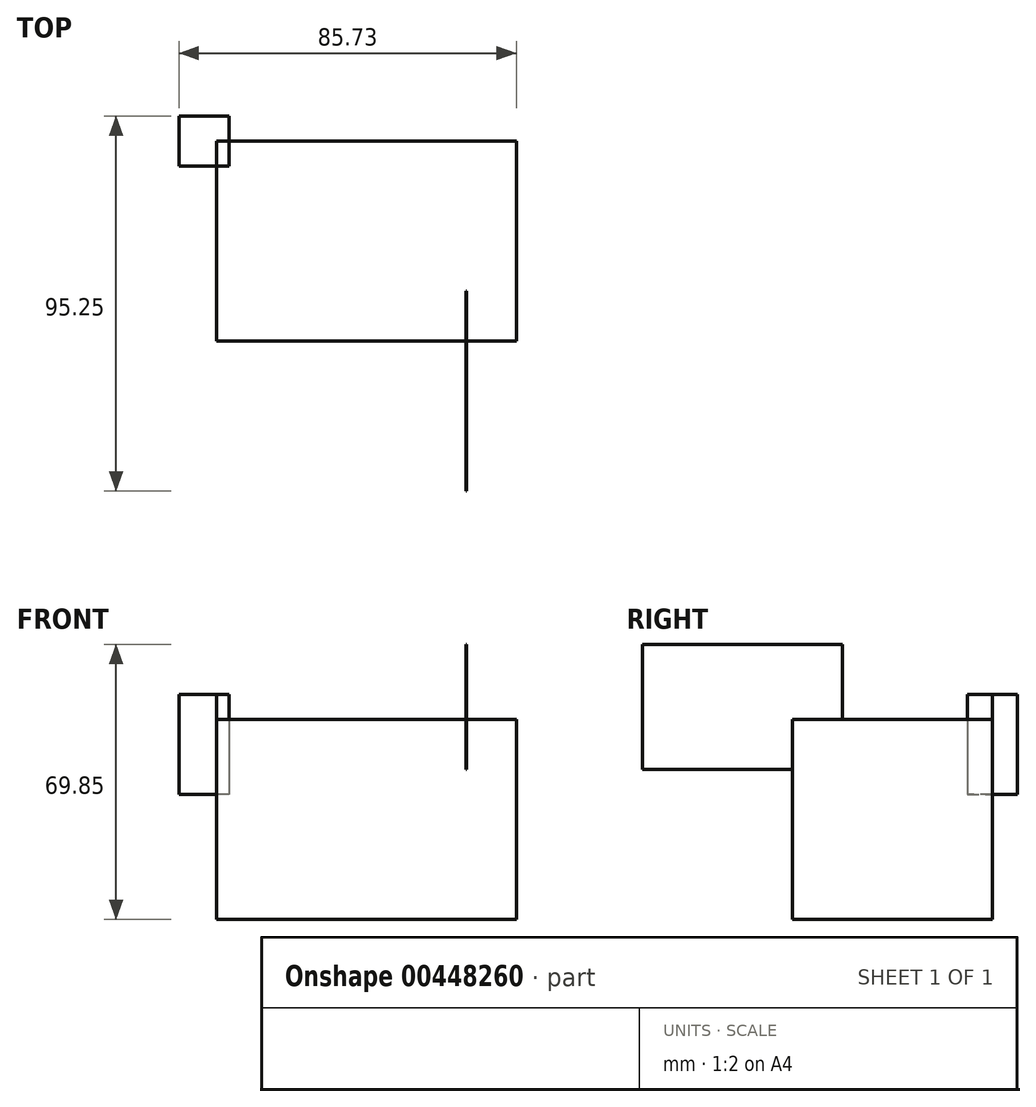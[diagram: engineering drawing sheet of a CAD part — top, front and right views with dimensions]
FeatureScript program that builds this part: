
annotation { "Feature Type Name" : "Feature", "Feature Type Description" : "" }
export const myFeature = defineFeature(function(context is Context, id is Id, definition is map)
    precondition{}
    {
        {
            var Q0;
            Q0=qCreatedBy(makeId("Front.planeOp"),FACE);
            var sketch = newSketch(context, id + "F0", { "sketchPlane" : qUnion([Q0])});
            skLineSegment(sketch, "E0.bottom", {"start": v(-2.72, 1) * mm, "end": v(73.48, 1) * mm});
            skLineSegment(sketch, "E0.top", {"start": v(-2.72, 51.8) * mm, "end": v(73.48, 51.8) * mm});
            skLineSegment(sketch, "E0.left", {"start": v(-2.72, 1) * mm, "end": v(-2.72, 51.8) * mm});
            skLineSegment(sketch, "E0.right", {"start": v(73.48, 1) * mm, "end": v(73.48, 51.8) * mm});
            skSolve(sketch);
        }
        {
            var Q0;
            Q0 = qSketchRegion(id + "F0", true);
            extrude(context, id + "F1", {"entities" : qUnion([Q0]), "depth" : 50.8 * mm});
        }
        {
            var Q0;
            Q0=makeQuery(id+"F1.opExtrude","CAP_FACE",FACE,{"disambiguationData":[OSD([sQuery(id+"F0.wireOp",EDGE,"E0.bottom"),sQuery(id+"F0.wireOp",EDGE,"E0.top"),sQuery(id+"F0.wireOp",EDGE,"E0.left"),sQuery(id+"F0.wireOp",EDGE,"E0.right")])],"isStart":false});
            var sketch = newSketch(context, id + "F2", { "sketchPlane" : qUnion([Q0])});
            skLineSegment(sketch, "E1.bottom", {"start": v(60.78, 39.1) * mm, "end": v(60.62, 39.1) * mm});
            skLineSegment(sketch, "E1.top", {"start": v(60.78, 51.8) * mm, "end": v(60.62, 51.8) * mm});
            skLineSegment(sketch, "E1.left", {"start": v(60.78, 39.1) * mm, "end": v(60.78, 51.8) * mm});
            skLineSegment(sketch, "E1.right", {"start": v(60.62, 39.1) * mm, "end": v(60.62, 51.8) * mm});
            skSolve(sketch);
        }
        {
            var Q0;
            Q0=makeQuery(id+"F2.imprint","IMPRINT",FACE,{"disambiguationData":[TD([[makeQuery(id+"F2.imprint","IMPRINT",EDGE,{"derivedFrom":sQuery(id+"F2.wireOp",EDGE,"E1.bottom")}),-1.0]])]});
            extrude(context, id + "F3", {"entities" : qUnion([Q0]), "operationType" : NewBodyOperationType.REMOVE, "oppositeDirection" : true, "depth" : 12.7 * mm});
        }
        {
            var Q0;
            Q0=makeQuery(id+"F3.boolean.opBoolean","COPY",FACE,{"derivedFrom":makeQuery(id+"F3.opExtrude","CAP_FACE",FACE,{"disambiguationData":[OSD([sQuery(id+"F2.wireOp",EDGE,"E1.bottom"),sQuery(id+"F2.wireOp",EDGE,"E1.top"),sQuery(id+"F2.wireOp",EDGE,"E1.left"),sQuery(id+"F2.wireOp",EDGE,"E1.right")])],"isStart":false})});
            var sketch = newSketch(context, id + "F4", { "sketchPlane" : qUnion([Q0])});
            skLineSegment(sketch, "E2.bottom", {"start": v(60.62, 70.86) * mm, "end": v(60.78, 70.86) * mm});
            skLineSegment(sketch, "E2.top", {"start": v(60.62, 39.1) * mm, "end": v(60.78, 39.1) * mm});
            skLineSegment(sketch, "E2.left", {"start": v(60.62, 70.86) * mm, "end": v(60.62, 39.1) * mm});
            skLineSegment(sketch, "E2.right", {"start": v(60.78, 70.86) * mm, "end": v(60.78, 39.1) * mm});
            skSolve(sketch);
        }
        {
            var Q0;
            {var subQ0=sQuery(id+"F4.wireOp",EDGE,"E2.bottom");Q0=makeQuery(id+"F4.imprint","IMPRINT",FACE,{"disambiguationData":[TD([[makeQuery(id+"F4.imprint","IMPRINT",EDGE,{"derivedFrom":subQ0}),-1.0]])]});}
            var Q1;
            {var subQ0=sQuery(id+"F4.wireOp",EDGE,"E2.top");Q1=makeQuery(id+"F4.imprint","IMPRINT",FACE,{"disambiguationData":[TD([[makeQuery(id+"F4.imprint","IMPRINT",EDGE,{"derivedFrom":subQ0}),-1.0]])]});}
            extrude(context, id + "F5", {"entities" : qUnion([Q0, Q1]), "operationType" : NewBodyOperationType.ADD, "depth" : 50.8 * mm});
        }
        {
            var Q0;
            Q0=makeQuery(id+"F1.opExtrude","SWEPT_FACE",FACE,{"disambiguationData":[OSD([sQuery(id+"F0.wireOp",EDGE,"E0.left")])]});
            var sketch = newSketch(context, id + "F6", { "sketchPlane" : qUnion([Q0])});
            skLineSegment(sketch, "E3.bottom", {"start": v(0, 51.8) * mm, "end": v(6.35, 51.8) * mm});
            skLineSegment(sketch, "E3.top", {"start": v(0, 32.76) * mm, "end": v(6.35, 32.76) * mm});
            skLineSegment(sketch, "E3.left", {"start": v(0, 51.8) * mm, "end": v(0, 32.76) * mm});
            skLineSegment(sketch, "E3.right", {"start": v(6.35, 51.8) * mm, "end": v(6.35, 32.76) * mm});
            skSolve(sketch);
        }
        {
            var Q0;
            Q0=makeQuery(id+"F6.imprint","IMPRINT",FACE,{"disambiguationData":[TD([[makeQuery(id+"F6.imprint","IMPRINT",EDGE,{"derivedFrom":sQuery(id+"F6.wireOp",EDGE,"E3.bottom")}),1.0]])]});
            extrude(context, id + "F7", {"entities" : qUnion([Q0]), "operationType" : NewBodyOperationType.REMOVE, "oppositeDirection" : true, "depth" : 3.17 * mm});
        }
        {
            var Q0;
            Q0=makeQuery(id+"F7.boolean.opBoolean","COPY",FACE,{"derivedFrom":makeQuery(id+"F7.opExtrude","SWEPT_FACE",FACE,{"disambiguationData":[OSD([sQuery(id+"F6.wireOp",EDGE,"E3.top")])]})});
            var sketch = newSketch(context, id + "F8", { "sketchPlane" : qUnion([Q0])});
            skLineSegment(sketch, "E4.bottom", {"start": v(0.45, -6.35) * mm, "end": v(-12.25, -6.35) * mm});
            skLineSegment(sketch, "E4.top", {"start": v(0.45, 6.35) * mm, "end": v(-12.25, 6.35) * mm});
            skLineSegment(sketch, "E4.left", {"start": v(0.45, -6.35) * mm, "end": v(0.45, 6.35) * mm});
            skLineSegment(sketch, "E4.right", {"start": v(-12.25, -6.35) * mm, "end": v(-12.25, 6.35) * mm});
            skSolve(sketch);
        }
        {
            var Q0;
            {var subQ3=sQuery(id+"F8.wireOp",EDGE,"E4.top");Q0=makeQuery(id+"F8.imprint","IMPRINT",FACE,{"disambiguationData":[TD([[makeQuery(id+"F8.imprint","IMPRINT",EDGE,{"derivedFrom":subQ3}),1.0]])]});}
            var Q1;
            {var subQ1=sQuery(id+"F6.wireOp",EDGE,"E3.top");var subQ2=makeQuery(id+"F7.boolean.opBoolean","COPY",EDGE,{"derivedFrom":makeQuery(id+"F7.opExtrude","CAP_EDGE",EDGE,{"disambiguationData":[OSD([subQ1])],"isStart":true})});Q1=makeQuery(id+"F8.imprint","IMPRINT",FACE,{"disambiguationData":[TD([[makeQuery(id+"F8.imprint","IMPRINT",EDGE,{"derivedFrom":subQ2}),1.0]])]});}
            extrude(context, id + "F9", {"entities" : qUnion([Q0, Q1]), "operationType" : NewBodyOperationType.ADD, "depth" : 25.4 * mm});
        }
    });
